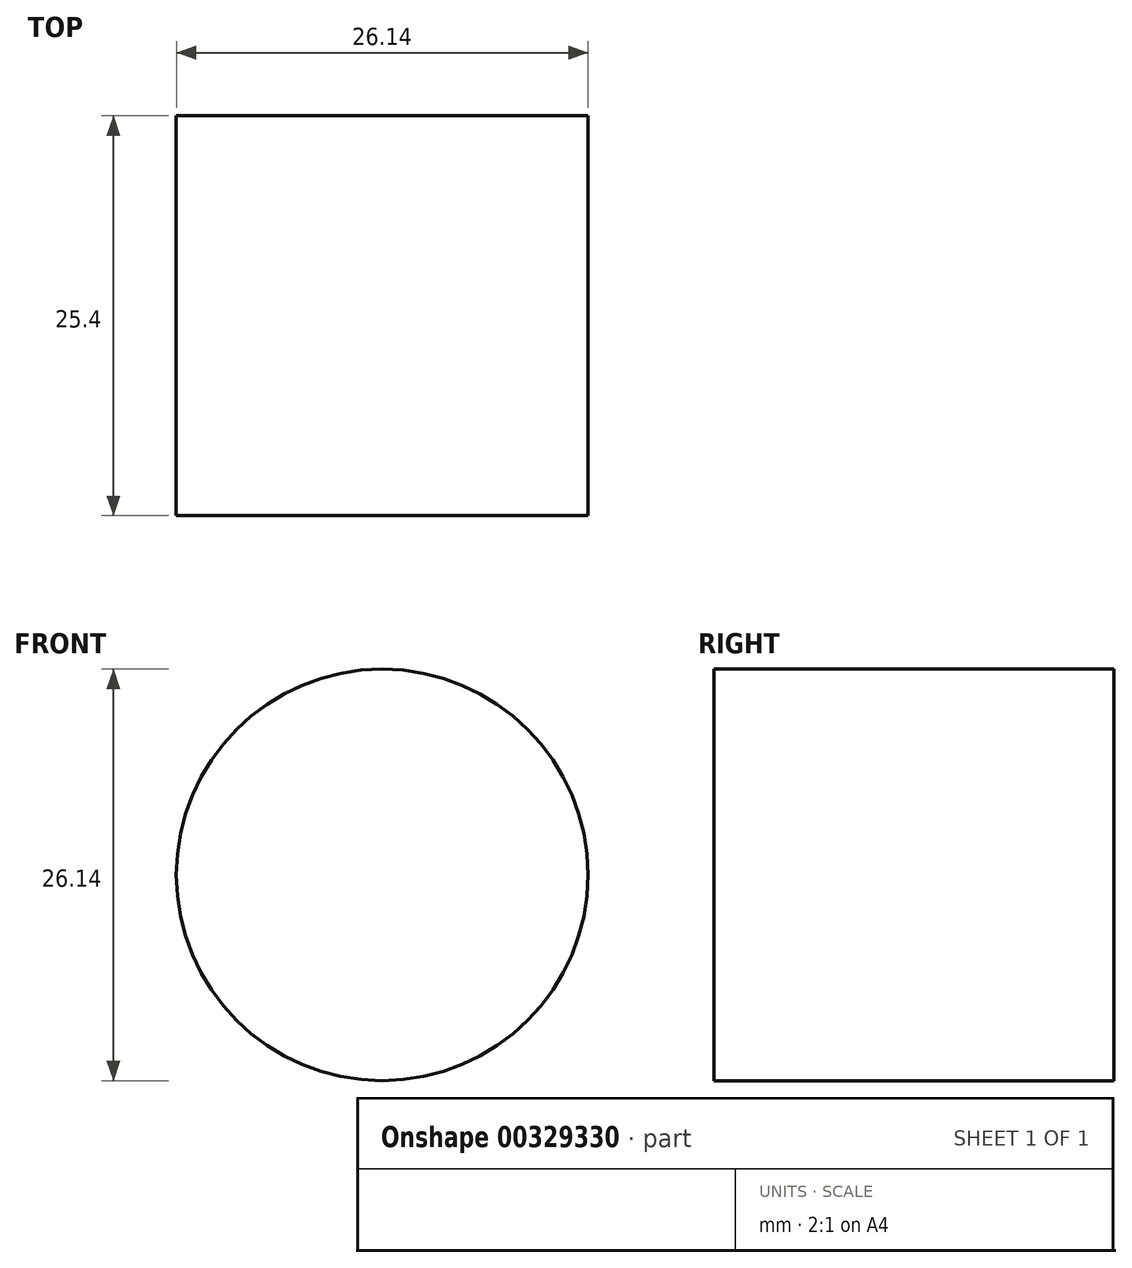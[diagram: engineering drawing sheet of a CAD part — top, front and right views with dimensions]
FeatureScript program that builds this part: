
annotation { "Feature Type Name" : "Feature", "Feature Type Description" : "" }
export const myFeature = defineFeature(function(context is Context, id is Id, definition is map)
    precondition{}
    {
        {
            var Q0;
            Q0=qCreatedBy(makeId("Front.planeOp"),FACE);
            var sketch = newSketch(context, id + "F0", { "sketchPlane" : qUnion([Q0])});
            skCircle(sketch, "E0", {"center": v(0, 0) * mm, "radius": 1.3 * mm});
            skCircle(sketch, "E1", {"center": v(0, -28.55) * mm, "radius": 5.56 * mm});
            skCircle(sketch, "E2", {"center": v(13.02, -28.72) * mm, "radius": 13.07 * mm});
            skSolve(sketch);
        }
        {
            var Q0;
            Q0=sQuery(id+"F0.wireOp",EDGE,"E2");
            extrude(context, id + "F1", {"bodyType" : ToolBodyType.SURFACE, "surfaceEntities" : qUnion([Q0]), "depth" : 25.4 * mm});
        }
    });
